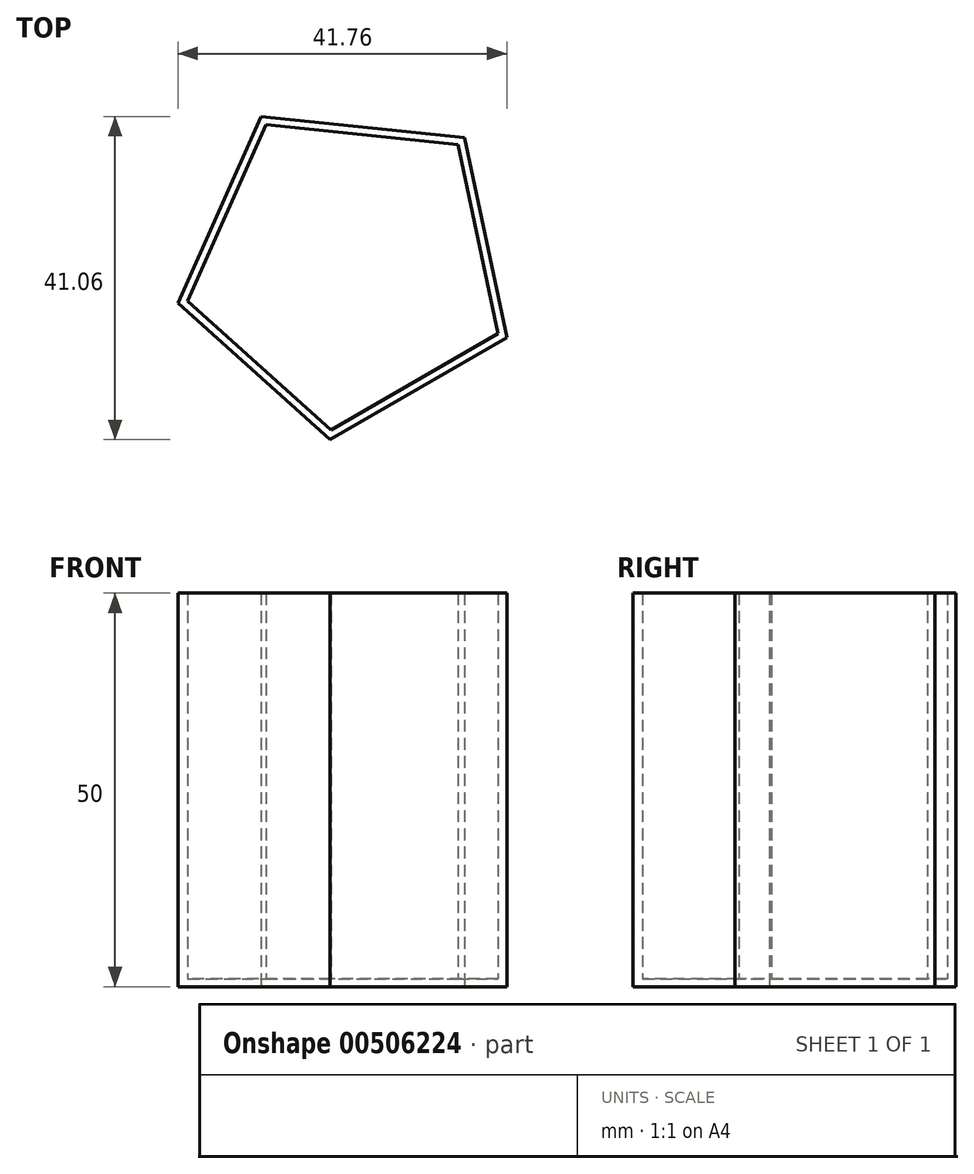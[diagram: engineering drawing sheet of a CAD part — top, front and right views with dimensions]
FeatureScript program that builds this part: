
annotation { "Feature Type Name" : "Feature", "Feature Type Description" : "" }
export const myFeature = defineFeature(function(context is Context, id is Id, definition is map)
    precondition{}
    {
        {
            var Q0;
            Q0=qCreatedBy(makeId("Top.planeOp"),FACE);
            var sketch = newSketch(context, id + "F0", { "sketchPlane" : qUnion([Q0])});
            skCircle(sketch, "E0.cCircle", {"center": v(0, 0) * mm, "radius": 17.86 * mm, "construction": true});
            skLineSegment(sketch, "E0.0", {"start": v(20.17, -8.97) * mm, "end": v(-2.3, -21.95) * mm});
            skLineSegment(sketch, "E0.1", {"start": v(-2.3, -21.95) * mm, "end": v(-21.59, -4.6) * mm});
            skLineSegment(sketch, "E0.2", {"start": v(-21.59, -4.6) * mm, "end": v(-11.05, 19.1) * mm});
            skLineSegment(sketch, "E0.3", {"start": v(-11.05, 19.1) * mm, "end": v(14.76, 16.41) * mm});
            skLineSegment(sketch, "E0.4", {"start": v(14.76, 16.41) * mm, "end": v(20.17, -8.97) * mm});
            skPoint(sketch, "E0.0.midPoint", {"position": v(8.94, -15.46) * mm});
            skSolve(sketch);
        }
        {
            var Q0;
            Q0=makeQuery(id+"F0.imprint","IMPRINT",FACE,{"disambiguationData":[TD([[makeQuery(id+"F0.imprint","IMPRINT",EDGE,{"derivedFrom":sQuery(id+"F0.wireOp",EDGE,"E0.0")}),-1.0]])]});
            extrude(context, id + "F1", {"entities" : qUnion([Q0]), "depth" : 50 * mm});
        }
        {
            var Q0;
            Q0=makeQuery(id+"F1.opExtrude","CAP_FACE",FACE,{"disambiguationData":[OSD([sQuery(id+"F0.wireOp",EDGE,"E0.0"),sQuery(id+"F0.wireOp",EDGE,"E0.1"),sQuery(id+"F0.wireOp",EDGE,"E0.2"),sQuery(id+"F0.wireOp",EDGE,"E0.3"),sQuery(id+"F0.wireOp",EDGE,"E0.4")])],"isStart":false});
            shell(context, id + "F2", {"entities" : qUnion([Q0]), "thickness" : 1 * mm});
        }
    });
